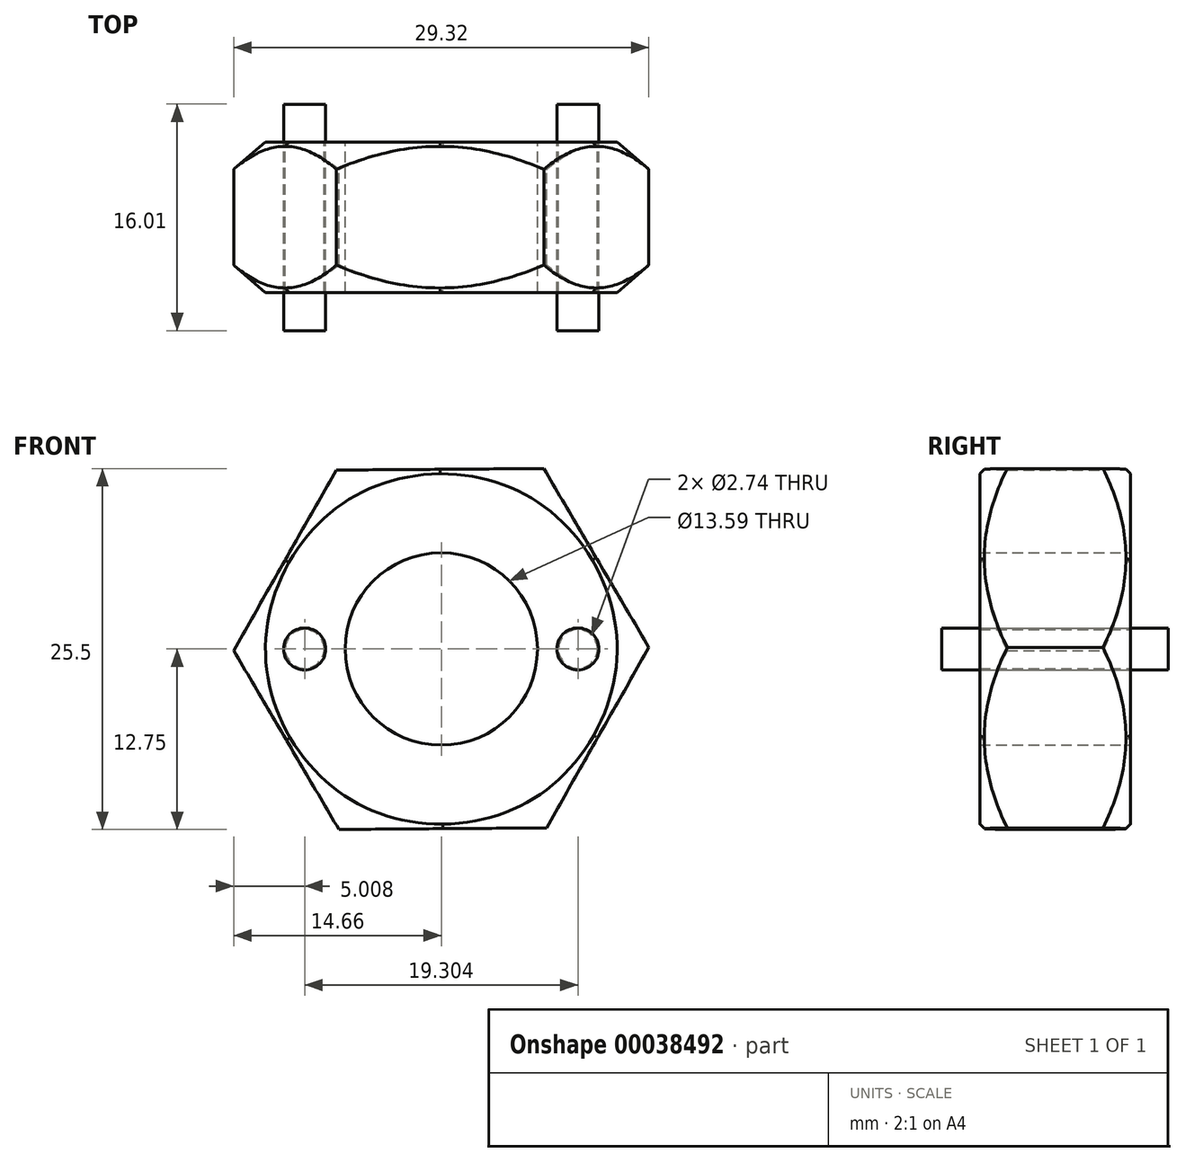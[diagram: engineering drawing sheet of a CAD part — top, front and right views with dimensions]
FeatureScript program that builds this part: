
annotation { "Feature Type Name" : "Feature", "Feature Type Description" : "" }
export const myFeature = defineFeature(function(context is Context, id is Id, definition is map)
    precondition{}
    {
        {
            var Q0;
            Q0=qCreatedBy(makeId("Front.planeOp"),FACE);
            var sketch = newSketch(context, id + "F0", { "sketchPlane" : qUnion([Q0])});
            skCircle(sketch, "E0.cCircle", {"center": v(0, 0) * mm, "radius": 12.7 * mm, "construction": true});
            skLineSegment(sketch, "E0.0", {"start": v(14.66, 0.1) * mm, "end": v(7.43, -12.64) * mm});
            skLineSegment(sketch, "E0.1", {"start": v(7.43, -12.64) * mm, "end": v(-7.24, -12.75) * mm});
            skLineSegment(sketch, "E0.2", {"start": v(-7.24, -12.75) * mm, "end": v(-14.66, -0.1) * mm});
            skLineSegment(sketch, "E0.3", {"start": v(-14.66, -0.1) * mm, "end": v(-7.43, 12.64) * mm});
            skLineSegment(sketch, "E0.4", {"start": v(-7.43, 12.64) * mm, "end": v(7.24, 12.75) * mm});
            skLineSegment(sketch, "E0.5", {"start": v(7.24, 12.75) * mm, "end": v(14.66, 0.1) * mm});
            skPoint(sketch, "E0.0.midPoint", {"position": v(11.05, -6.27) * mm});
            skCircle(sketch, "E1", {"center": v(9.65, 0) * mm, "radius": 1.37 * mm});
            skCircle(sketch, "E2", {"center": v(-9.65, 0) * mm, "radius": 1.37 * mm});
            skCircle(sketch, "E3", {"center": v(0, 0) * mm, "radius": 6.8 * mm});
            skSolve(sketch);
        }
        {
            var Q0;
            Q0=makeQuery(id+"F0.imprint","IMPRINT",FACE,{"disambiguationData":[TD([[makeQuery(id+"F0.imprint","IMPRINT",EDGE,{"derivedFrom":sQuery(id+"F0.wireOp",EDGE,"E0.0")}),-1.0]])]});
            extrude(context, id + "F1", {"entities" : qUnion([Q0]), "depth" : 10.64 * mm});
        }
        {
            var Q0;
            Q0=qCreatedBy(makeId("Front.planeOp"),FACE);
            var sketch = newSketch(context, id + "F2", { "sketchPlane" : qUnion([Q0])});
            skCircle(sketch, "E4", {"center": v(-9.65, 0) * mm, "radius": 1.49 * mm});
            skCircle(sketch, "E5", {"center": v(9.65, 0) * mm, "radius": 1.49 * mm});
            skSolve(sketch);
        }
        {
            var Q0;
            Q0=makeQuery(id+"F2.imprint","IMPRINT",FACE,{"disambiguationData":[TD([[makeQuery(id+"F2.imprint","IMPRINT",EDGE,{"derivedFrom":sQuery(id+"F2.wireOp",EDGE,"E5")}),1.0]])]});
            var Q1;
            Q1=makeQuery(id+"F2.imprint","IMPRINT",FACE,{"disambiguationData":[TD([[makeQuery(id+"F2.imprint","IMPRINT",EDGE,{"derivedFrom":sQuery(id+"F2.wireOp",EDGE,"E4")}),1.0]])]});
            extrude(context, id + "F3", {"entities" : qUnion([Q0, Q1]), "depth" : 13.33 * mm, "hasSecondDirection" : true, "secondDirectionOppositeDirection" : true, "secondDirectionDepth" : 2.67 * mm});
        }
        {
            var Q0;
            Q0=makeQuery(id+"F1.opExtrude","CAP_EDGE",EDGE,{"disambiguationData":[OSD([sQuery(id+"F0.wireOp",EDGE,"E0.3")])],"isStart":false});
            var Q1;
            Q1=makeQuery(id+"F1.opExtrude","CAP_EDGE",EDGE,{"disambiguationData":[OSD([sQuery(id+"F0.wireOp",EDGE,"E0.4")])],"isStart":false});
            var Q2;
            Q2=makeQuery(id+"F1.opExtrude","CAP_EDGE",EDGE,{"disambiguationData":[OSD([sQuery(id+"F0.wireOp",EDGE,"E0.2")])],"isStart":false});
            var Q3;
            Q3=makeQuery(id+"F1.opExtrude","CAP_EDGE",EDGE,{"disambiguationData":[OSD([sQuery(id+"F0.wireOp",EDGE,"E0.1")])],"isStart":false});
            var Q4;
            Q4=makeQuery(id+"F1.opExtrude","CAP_EDGE",EDGE,{"disambiguationData":[OSD([sQuery(id+"F0.wireOp",EDGE,"E0.0")])],"isStart":false});
            var Q5;
            Q5=makeQuery(id+"F1.opExtrude","CAP_EDGE",EDGE,{"disambiguationData":[OSD([sQuery(id+"F0.wireOp",EDGE,"E0.5")])],"isStart":false});
            var Q6;
            Q6=makeQuery(id+"F1.opExtrude","CAP_EDGE",EDGE,{"disambiguationData":[OSD([sQuery(id+"F0.wireOp",EDGE,"E0.4")])],"isStart":true});
            var Q7;
            Q7=makeQuery(id+"F1.opExtrude","CAP_EDGE",EDGE,{"disambiguationData":[OSD([sQuery(id+"F0.wireOp",EDGE,"E0.5")])],"isStart":true});
            var Q8;
            Q8=makeQuery(id+"F1.opExtrude","CAP_EDGE",EDGE,{"disambiguationData":[OSD([sQuery(id+"F0.wireOp",EDGE,"E0.0")])],"isStart":true});
            var Q9;
            Q9=makeQuery(id+"F1.opExtrude","CAP_EDGE",EDGE,{"disambiguationData":[OSD([sQuery(id+"F0.wireOp",EDGE,"E0.1")])],"isStart":true});
            var Q10;
            Q10=makeQuery(id+"F1.opExtrude","CAP_EDGE",EDGE,{"disambiguationData":[OSD([sQuery(id+"F0.wireOp",EDGE,"E0.2")])],"isStart":true});
            var Q11;
            Q11=makeQuery(id+"F1.opExtrude","CAP_EDGE",EDGE,{"disambiguationData":[OSD([sQuery(id+"F0.wireOp",EDGE,"E0.3")])],"isStart":true});
            chamfer(context, id + "F4", {"entities" : qUnion([Q0, Q1, Q2, Q3, Q4, Q5, Q6, Q7, Q8, Q9, Q10, Q11]), "chamferType" : ChamferType.OFFSET_ANGLE, "width" : 0.32 * mm, "oppositeDirection" : false, "angle" : 45 * degree, "tangentPropagation" : true});
        }
        {
            var Q0;
            Q0=makeQuery(id+"F4.opChamfer","BLEND_EDGE",EDGE,{"blendedFrom":[makeQuery(id+"F1.opExtrude","CAP_EDGE",EDGE,{"disambiguationData":[OSD([sQuery(id+"F0.wireOp",EDGE,"E0.0")])],"isStart":true}),makeQuery(id+"F1.opExtrude","CAP_EDGE",EDGE,{"disambiguationData":[OSD([sQuery(id+"F0.wireOp",EDGE,"E0.5")])],"isStart":true})],"blendedInto":[]});
            var Q1;
            Q1=makeQuery(id+"F4.opChamfer","BLEND_EDGE",EDGE,{"blendedFrom":[makeQuery(id+"F1.opExtrude","CAP_EDGE",EDGE,{"disambiguationData":[OSD([sQuery(id+"F0.wireOp",EDGE,"E0.0")])],"isStart":true}),makeQuery(id+"F1.opExtrude","CAP_EDGE",EDGE,{"disambiguationData":[OSD([sQuery(id+"F0.wireOp",EDGE,"E0.1")])],"isStart":true})],"blendedInto":[]});
            var Q2;
            Q2=makeQuery(id+"F4.opChamfer","BLEND_EDGE",EDGE,{"blendedFrom":[makeQuery(id+"F1.opExtrude","CAP_EDGE",EDGE,{"disambiguationData":[OSD([sQuery(id+"F0.wireOp",EDGE,"E0.1")])],"isStart":true}),makeQuery(id+"F1.opExtrude","CAP_EDGE",EDGE,{"disambiguationData":[OSD([sQuery(id+"F0.wireOp",EDGE,"E0.2")])],"isStart":true})],"blendedInto":[]});
            var Q3;
            Q3=makeQuery(id+"F4.opChamfer","BLEND_EDGE",EDGE,{"blendedFrom":[makeQuery(id+"F1.opExtrude","CAP_EDGE",EDGE,{"disambiguationData":[OSD([sQuery(id+"F0.wireOp",EDGE,"E0.2")])],"isStart":true}),makeQuery(id+"F1.opExtrude","CAP_EDGE",EDGE,{"disambiguationData":[OSD([sQuery(id+"F0.wireOp",EDGE,"E0.3")])],"isStart":true})],"blendedInto":[]});
            var Q4;
            Q4=makeQuery(id+"F4.opChamfer","BLEND_EDGE",EDGE,{"blendedFrom":[makeQuery(id+"F1.opExtrude","CAP_EDGE",EDGE,{"disambiguationData":[OSD([sQuery(id+"F0.wireOp",EDGE,"E0.3")])],"isStart":true}),makeQuery(id+"F1.opExtrude","CAP_EDGE",EDGE,{"disambiguationData":[OSD([sQuery(id+"F0.wireOp",EDGE,"E0.4")])],"isStart":true})],"blendedInto":[]});
            var Q5;
            Q5=makeQuery(id+"F4.opChamfer","BLEND_EDGE",EDGE,{"blendedFrom":[makeQuery(id+"F1.opExtrude","CAP_EDGE",EDGE,{"disambiguationData":[OSD([sQuery(id+"F0.wireOp",EDGE,"E0.4")])],"isStart":true}),makeQuery(id+"F1.opExtrude","CAP_EDGE",EDGE,{"disambiguationData":[OSD([sQuery(id+"F0.wireOp",EDGE,"E0.5")])],"isStart":true})],"blendedInto":[]});
            var Q6;
            Q6=makeQuery(id+"F4.opChamfer","BLEND_EDGE",EDGE,{"blendedFrom":[makeQuery(id+"F1.opExtrude","CAP_EDGE",EDGE,{"disambiguationData":[OSD([sQuery(id+"F0.wireOp",EDGE,"E0.2")])],"isStart":false}),makeQuery(id+"F1.opExtrude","CAP_EDGE",EDGE,{"disambiguationData":[OSD([sQuery(id+"F0.wireOp",EDGE,"E0.3")])],"isStart":false})],"blendedInto":[]});
            var Q7;
            Q7=makeQuery(id+"F4.opChamfer","BLEND_EDGE",EDGE,{"blendedFrom":[makeQuery(id+"F1.opExtrude","CAP_EDGE",EDGE,{"disambiguationData":[OSD([sQuery(id+"F0.wireOp",EDGE,"E0.1")])],"isStart":false}),makeQuery(id+"F1.opExtrude","CAP_EDGE",EDGE,{"disambiguationData":[OSD([sQuery(id+"F0.wireOp",EDGE,"E0.2")])],"isStart":false})],"blendedInto":[]});
            var Q8;
            Q8=makeQuery(id+"F4.opChamfer","BLEND_EDGE",EDGE,{"blendedFrom":[makeQuery(id+"F1.opExtrude","CAP_EDGE",EDGE,{"disambiguationData":[OSD([sQuery(id+"F0.wireOp",EDGE,"E0.3")])],"isStart":false}),makeQuery(id+"F1.opExtrude","CAP_EDGE",EDGE,{"disambiguationData":[OSD([sQuery(id+"F0.wireOp",EDGE,"E0.4")])],"isStart":false})],"blendedInto":[]});
            var Q9;
            Q9=makeQuery(id+"F4.opChamfer","BLEND_EDGE",EDGE,{"blendedFrom":[makeQuery(id+"F1.opExtrude","CAP_EDGE",EDGE,{"disambiguationData":[OSD([sQuery(id+"F0.wireOp",EDGE,"E0.4")])],"isStart":false}),makeQuery(id+"F1.opExtrude","CAP_EDGE",EDGE,{"disambiguationData":[OSD([sQuery(id+"F0.wireOp",EDGE,"E0.5")])],"isStart":false})],"blendedInto":[]});
            var Q10;
            Q10=makeQuery(id+"F4.opChamfer","BLEND_EDGE",EDGE,{"blendedFrom":[makeQuery(id+"F1.opExtrude","CAP_EDGE",EDGE,{"disambiguationData":[OSD([sQuery(id+"F0.wireOp",EDGE,"E0.0")])],"isStart":false}),makeQuery(id+"F1.opExtrude","CAP_EDGE",EDGE,{"disambiguationData":[OSD([sQuery(id+"F0.wireOp",EDGE,"E0.5")])],"isStart":false})],"blendedInto":[]});
            var Q11;
            Q11=makeQuery(id+"F4.opChamfer","BLEND_EDGE",EDGE,{"blendedFrom":[makeQuery(id+"F1.opExtrude","CAP_EDGE",EDGE,{"disambiguationData":[OSD([sQuery(id+"F0.wireOp",EDGE,"E0.0")])],"isStart":false}),makeQuery(id+"F1.opExtrude","CAP_EDGE",EDGE,{"disambiguationData":[OSD([sQuery(id+"F0.wireOp",EDGE,"E0.1")])],"isStart":false})],"blendedInto":[]});
            fillet(context, id + "F5", {"entities" : qUnion([Q0, Q1, Q2, Q3, Q4, Q5, Q6, Q7, Q8, Q9, Q10, Q11]), "radius" : 17.78 * mm, "tangentPropagation" : true, "allowEdgeOverflow" : false});
        }
    });
